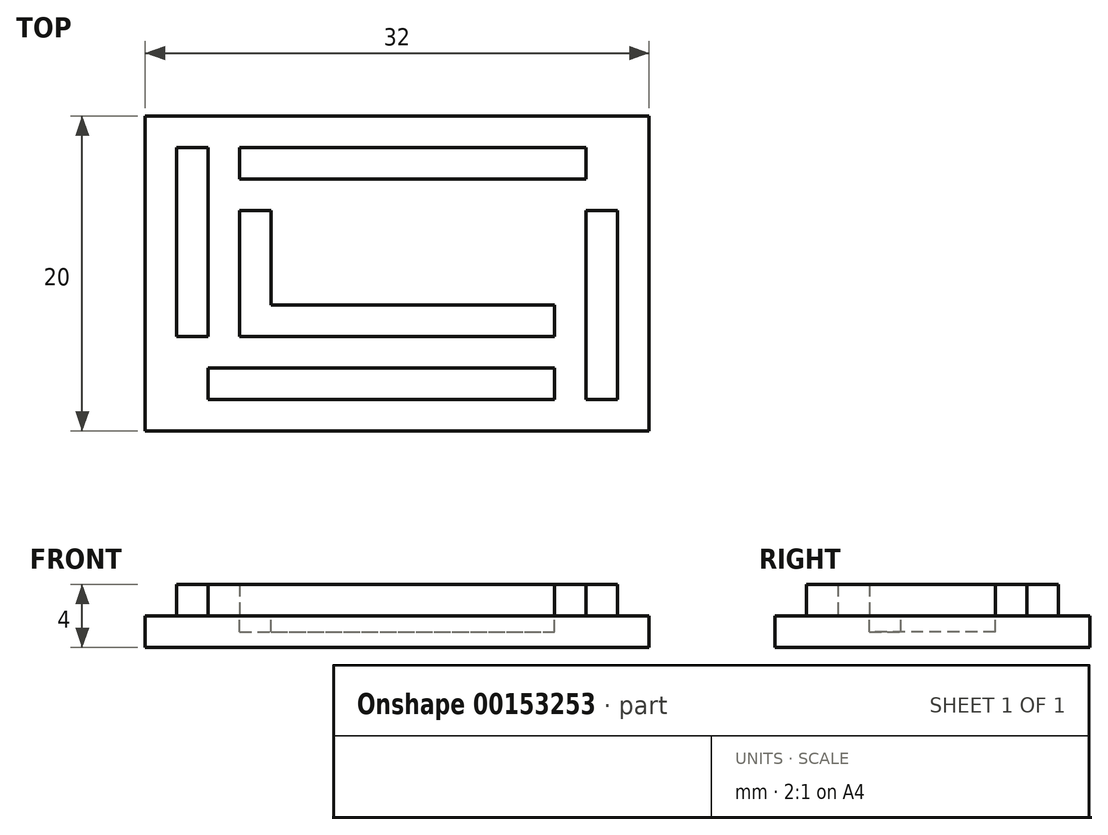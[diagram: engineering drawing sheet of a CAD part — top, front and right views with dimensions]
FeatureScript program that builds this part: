
annotation { "Feature Type Name" : "Feature", "Feature Type Description" : "" }
export const myFeature = defineFeature(function(context is Context, id is Id, definition is map)
    precondition{}
    {
        {
            assignVariable(context, id + "F0", {"name" : "T", "anyValue" : 2});
        }
        {
            var Q0;
            Q0=qCreatedBy(makeId("Top.planeOp"),FACE);
            var sketch = newSketch(context, id + "F1", { "sketchPlane" : qUnion([Q0])});
            skLineSegment(sketch, "E0.bottom", {"start": v(16, -10) * mm, "end": v(-16, -10) * mm});
            skLineSegment(sketch, "E0.top", {"start": v(16, 10) * mm, "end": v(-16, 10) * mm});
            skLineSegment(sketch, "E0.left", {"start": v(16, -10) * mm, "end": v(16, 10) * mm});
            skLineSegment(sketch, "E0.right", {"start": v(-16, -10) * mm, "end": v(-16, 10) * mm});
            skPoint(sketch, "E0.middle", {"position": v(0, 0) * mm});
            skSolve(sketch);
        }
        {
            var Q0;
            Q0=makeQuery(id+"F1.imprint","IMPRINT",FACE,{"disambiguationData":[TD([[makeQuery(id+"F1.imprint","IMPRINT",EDGE,{"derivedFrom":sQuery(id+"F1.wireOp",EDGE,"E0.bottom")}),-1.0]])]});
            extrude(context, id + "F2", {"entities" : qUnion([Q0]), "depth" : (getVariable(context, 'T')) * mm});
        }
        {
            var Q0;
            Q0=makeQuery(id+"F2.opExtrude","CAP_FACE",FACE,{"disambiguationData":[OSD([sQuery(id+"F1.wireOp",EDGE,"E0.bottom"),sQuery(id+"F1.wireOp",EDGE,"E0.top"),sQuery(id+"F1.wireOp",EDGE,"E0.left"),sQuery(id+"F1.wireOp",EDGE,"E0.right")])],"isStart":false});
            var sketch = newSketch(context, id + "F3", { "sketchPlane" : qUnion([Q0])});
            skLineSegment(sketch, "E1.0", {"start": v(-14, -8) * mm, "end": v(14, -8) * mm, "construction": true});
            skLineSegment(sketch, "E1.1", {"start": v(-14, 8) * mm, "end": v(-14, -8) * mm, "construction": true});
            skLineSegment(sketch, "E1.2", {"start": v(14, 8) * mm, "end": v(-14, 8) * mm, "construction": true});
            skLineSegment(sketch, "E1.3", {"start": v(14, -8) * mm, "end": v(14, 8) * mm, "construction": true});
            skLineSegment(sketch, "E2.bottom", {"start": v(-14, 8) * mm, "end": v(-12, 8) * mm});
            skLineSegment(sketch, "E2.top", {"start": v(-14, -4) * mm, "end": v(-12, -4) * mm});
            skLineSegment(sketch, "E2.left", {"start": v(-14, 8) * mm, "end": v(-14, -4) * mm});
            skLineSegment(sketch, "E2.right", {"start": v(-12, 8) * mm, "end": v(-12, -4) * mm});
            skLineSegment(sketch, "E3.bottom", {"start": v(14, -8) * mm, "end": v(12, -8) * mm});
            skLineSegment(sketch, "E3.top", {"start": v(14, 4) * mm, "end": v(12, 4) * mm});
            skLineSegment(sketch, "E3.left", {"start": v(14, -8) * mm, "end": v(14, 4) * mm});
            skLineSegment(sketch, "E3.right", {"start": v(12, -8) * mm, "end": v(12, 4) * mm});
            skLineSegment(sketch, "E4.bottom", {"start": v(12, 8) * mm, "end": v(-10, 8) * mm});
            skLineSegment(sketch, "E4.top", {"start": v(12, 6) * mm, "end": v(-10, 6) * mm});
            skLineSegment(sketch, "E4.left", {"start": v(12, 8) * mm, "end": v(12, 6) * mm});
            skLineSegment(sketch, "E4.right", {"start": v(-10, 8) * mm, "end": v(-10, 6) * mm});
            skLineSegment(sketch, "E5.bottom", {"start": v(-12, -8) * mm, "end": v(10, -8) * mm});
            skLineSegment(sketch, "E5.top", {"start": v(-12, -6) * mm, "end": v(10, -6) * mm});
            skLineSegment(sketch, "E5.left", {"start": v(-12, -8) * mm, "end": v(-12, -6) * mm});
            skLineSegment(sketch, "E5.right", {"start": v(10, -8) * mm, "end": v(10, -6) * mm});
            skSolve(sketch);
        }
        {
            var Q0;
            Q0=makeQuery(id+"F3.imprint","IMPRINT",FACE,{"disambiguationData":[TD([[makeQuery(id+"F3.imprint","IMPRINT",EDGE,{"derivedFrom":sQuery(id+"F3.wireOp",EDGE,"E2.bottom")}),-1.0]])]});
            var Q1;
            Q1=makeQuery(id+"F3.imprint","IMPRINT",FACE,{"disambiguationData":[TD([[makeQuery(id+"F3.imprint","IMPRINT",EDGE,{"derivedFrom":sQuery(id+"F3.wireOp",EDGE,"E4.bottom")}),1.0]])]});
            var Q2;
            Q2=makeQuery(id+"F3.imprint","IMPRINT",FACE,{"disambiguationData":[TD([[makeQuery(id+"F3.imprint","IMPRINT",EDGE,{"derivedFrom":sQuery(id+"F3.wireOp",EDGE,"E3.bottom")}),-1.0]])]});
            var Q3;
            Q3=makeQuery(id+"F3.imprint","IMPRINT",FACE,{"disambiguationData":[TD([[makeQuery(id+"F3.imprint","IMPRINT",EDGE,{"derivedFrom":sQuery(id+"F3.wireOp",EDGE,"E5.bottom")}),1.0]])]});
            extrude(context, id + "F4", {"entities" : qUnion([Q0, Q1, Q2, Q3]), "operationType" : NewBodyOperationType.ADD, "depth" : (getVariable(context, 'T')) * mm});
        }
        {
            var Q0;
            Q0=makeQuery(id+"F2.opExtrude","CAP_FACE",FACE,{"disambiguationData":[OSD([sQuery(id+"F1.wireOp",EDGE,"E0.bottom"),sQuery(id+"F1.wireOp",EDGE,"E0.top"),sQuery(id+"F1.wireOp",EDGE,"E0.left"),sQuery(id+"F1.wireOp",EDGE,"E0.right")])],"isStart":false});
            var sketch = newSketch(context, id + "F5", { "sketchPlane" : qUnion([Q0])});
            skLineSegment(sketch, "E6.bottom", {"start": v(10, 4) * mm, "end": v(-10, 4) * mm, "construction": true});
            skLineSegment(sketch, "E6.top", {"start": v(10, -4) * mm, "end": v(-10, -4) * mm, "construction": true});
            skLineSegment(sketch, "E6.left", {"start": v(10, 4) * mm, "end": v(10, -4) * mm, "construction": true});
            skLineSegment(sketch, "E6.right", {"start": v(-10, 4) * mm, "end": v(-10, -4) * mm, "construction": true});
            skPoint(sketch, "E6.middle", {"position": v(0, 0) * mm});
            skLineSegment(sketch, "E7.bottom", {"start": v(-10, -4) * mm, "end": v(10, -4) * mm});
            skLineSegment(sketch, "E7.top", {"start": v(-10, -2) * mm, "end": v(10, -2) * mm});
            skLineSegment(sketch, "E7.left", {"start": v(-10, -4) * mm, "end": v(-10, -2) * mm});
            skLineSegment(sketch, "E7.right", {"start": v(10, -4) * mm, "end": v(10, -2) * mm});
            skLineSegment(sketch, "E8.bottom", {"start": v(-10, 4) * mm, "end": v(-8, 4) * mm});
            skLineSegment(sketch, "E8.top", {"start": v(-10, -2) * mm, "end": v(-8, -2) * mm});
            skLineSegment(sketch, "E8.left", {"start": v(-10, 4) * mm, "end": v(-10, -2) * mm});
            skLineSegment(sketch, "E8.right", {"start": v(-8, 4) * mm, "end": v(-8, -2) * mm});
            skLineSegment(sketch, "E9.bottom", {"start": v(10, -2) * mm, "end": v(8, -2) * mm});
            skLineSegment(sketch, "E9.top", {"start": v(10, 4) * mm, "end": v(8, 4) * mm});
            skLineSegment(sketch, "E9.left", {"start": v(10, -2) * mm, "end": v(10, 4) * mm});
            skLineSegment(sketch, "E9.right", {"start": v(8, -2) * mm, "end": v(8, 4) * mm});
            skSolve(sketch);
        }
        {
            var Q0;
            Q0=makeQuery(id+"F5.imprint","IMPRINT",FACE,{"disambiguationData":[TD([[makeQuery(id+"F5.imprint","IMPRINT",EDGE,{"derivedFrom":sQuery(id+"F5.wireOp",EDGE,"E8.bottom")}),-1.0]])]});
            var Q1;
            Q1=makeQuery(id+"F5.imprint","IMPRINT",FACE,{"disambiguationData":[TD([[makeQuery(id+"F5.imprint","IMPRINT",EDGE,{"derivedFrom":sQuery(id+"F5.wireOp",EDGE,"E7.bottom")}),1.0]])]});
            var Q2;
            Q2=makeQuery(id+"F5.imprint","IMPRINT",FACE,{"disambiguationData":[TD([[makeQuery(id+"F5.imprint","IMPRINT",EDGE,{"derivedFrom":sQuery(id+"F5.wireOp",EDGE,"E9.bottom")}),-1.0]])]});
            extrude(context, id + "F6", {"entities" : qUnion([Q0, Q1, Q2]), "operationType" : NewBodyOperationType.REMOVE, "oppositeDirection" : true, "depth" : 1 * mm});
        }
    });
